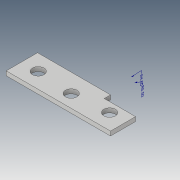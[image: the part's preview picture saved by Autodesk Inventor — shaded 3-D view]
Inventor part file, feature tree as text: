
AUTODESK INVENTOR PART (.ipt)
format: ipt  version: 2019 (Build 230136000, 136)  size: 371,200 bytes
history: native  units: mm
features: extrude x16, sketch x15, move_body x7, plane x6, direct_edit x6, projected_geometry x5, other x3, fillet x2, split x2, boolean_combine x1
ambient origin geometry x8: Origin, YZ Plane, XZ Plane, XY Plane, X Axis, Y Axis, Z Axis, Center Point
bodies: Solid1 (feature_tree), Solid2 (feature_tree), Solid3 (feature_tree), Solid4 (feature_tree), Solid5 (feature_tree)
feature tree (63):
  other  "Annotations"
  extrude  "Extrusion1"  Depth=45.0mm
  extrude  "Extrusion4"  Depth=5.0mm
  fillet  "Fillet1"  Radius=11.0mm
  extrude  "Extrusion5"  Depth=23.0mm
  plane  "Work Plane1"
  extrude  "Extrusion6"  Depth=10.0mm
  direct_edit  "Direct Edit1"
  extrude  "Extrusion7"  Depth=12.0mm
  fillet  "Fillet2"  Radius=5.0mm
  plane  "Work Plane5"
  extrude  "Extrusion8"  Depth=5.0mm
  plane  "Work Plane6"
  extrude  "Extrusion9"  Depth=17.8mm
  sketch  "Sketch12"  dims[d34=5.0mm d35=17.8mm]
  extrude  "Extrusion12"  Depth=17.8mm
  extrude  "Extrusion13"  Depth=30.8mm
  extrude  "Extrusion15"  Depth=3.0mm TaperAngle=0.0deg
  plane  "Work Plane7"
  extrude  "Extrusion16"  TaperAngle=0.0deg  [1 undecoded]
  extrude  "Extrusion17"  Depth=18.0mm
  plane  "Work Plane8"
  plane  "Work Plane9"
  split  "Split1"
  split  "Split2"
  boolean_combine  "Combine1"
  direct_edit  "Direct Edit2"
  extrude  "Extrusion22"  Depth=2.0mm
  sketch  "Sketch21"  dims[d52=18.0mm d53=11.0mm]
  extrude  "Extrusion23"  Depth=0.5mm TaperAngle=0.0deg
  extrude  "Extrusion24"  Depth=4.5mm TaperAngle=0.0deg
  direct_edit  "Direct Edit3"
  direct_edit  "Direct Edit4"
  direct_edit  "Direct Edit5"
  extrude  "Extrusion25"  Depth=4.5mm
  direct_edit  "Direct Edit6"
  sketch  "Sketch1"  dims[d0=6.0mm d1=0.0mm d4=45.0mm]
  sketch  "Sketch5"  dims[d5=5.0mm d6=5.0mm d7=11.0mm]
  sketch  "Sketch6"  dims[d8=11.0mm d9=23.0mm]
  sketch  "Sketch7"  dims[d10=10.0mm d20=13.0mm]
  sketch  "Sketch8"  dims[d24=3.0mm d25=0.0mm d26=12.0mm d27=5.0mm]
  sketch  "Sketch10"  dims[d28=3.0mm d29=0.0mm d33=5.0mm]
  projected_geometry  "Projected Loop2"
  sketch  "Sketch13"  dims[d36=8.0mm d37=17.8mm]
  sketch  "Sketch14"  dims[d38=7.1mm d39=30.8mm]
  sketch  "Sketch15"  dims[d40=7.1mm d41=3.0mm d42=0.0mm]
  sketch  "Sketch20"  dims[d46=0.0mm d47=0.0mm d48=-2.5mm d49=0.0mm d50=0.0mm d51=-2.5mm]
  projected_geometry  "Projected Loop6"
  projected_geometry  "Projected Loop7"
  sketch  "Sketch22"  dims[d54=2.0mm d55=0.0mm d56=2.0mm]
  projected_geometry  "Projected Loop8"
  sketch  "Sketch23"  dims[d57=0.0mm d58=0.5mm d59=0.0mm]
  sketch  "Sketch24"  dims[d60=0.0mm d61=7.25mm d62=0.0mm d68=5.0mm d69=7.25mm d70=0.0mm d72=2.0mm d73=10.0mm d74=0.0mm d80=10.0mm d81=0.0mm d82=15.0mm d83=3.0mm d88=-6.0mm d89=7.5mm d90=3.15mm d91=0.0mm d92=2.1mm d93=0.0mm d94=0.0mm d95=0.0mm d96=0.0mm d97=0.0mm d98=-0.3mm d113=2.1mm d114=0.0mm d115=1.4mm d116=0.0mm d117=1.4mm d118=0.0mm d119=0.0mm d120=0.0mm d121=0.8mm d122=0.0mm d123=0.0mm d124=1.76mm d125=0.0mm d126=0.0mm d127=-1.76mm d128=10.0mm d129=0.0mm d130=0.0mm d131=0.0mm d132=-2.76mm d84=49.911908mm d85=6.5mm d86=52.109261mm d87=4.5mm]
  projected_geometry  "Projected Loop9"
  move_body  "Move1"
  move_body  "Move2"
  move_body  "Move3"
  move_body  "Move4"
  move_body  "Move5"
  move_body  "Move6"
  move_body  "Move7"
  other  "Radial Dimension 1"
  other  "Radial Dimension 2"
note: 1 required parameter value undecoded (feature->parameter linkage not recoverable at this tier; creation-order binding heuristic only, values carry confidence <= 0.55)
